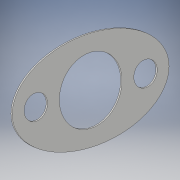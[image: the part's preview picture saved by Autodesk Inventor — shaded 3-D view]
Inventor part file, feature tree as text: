
AUTODESK INVENTOR PART (.ipt)
format: ipt  version: 2018 (Build 220112000, 112)  size: 108,032 bytes
history: native  units: mm
features: extrude x1, sketch x1
ambient origin geometry x8: Origin, YZ Plane, XZ Plane, XY Plane, X Axis, Y Axis, Z Axis, Center Point
bodies: Solid1 (feature_tree)
feature tree (2):
  extrude  "Extrusion1"  Depth=0.2mm
  sketch  "Sketch1"  dims[d0=3.0mm d1=8.0mm d3=7.0mm d4=7.0mm d5=20.0mm d6=12.0mm d7=0.2mm d8=0.0mm]
